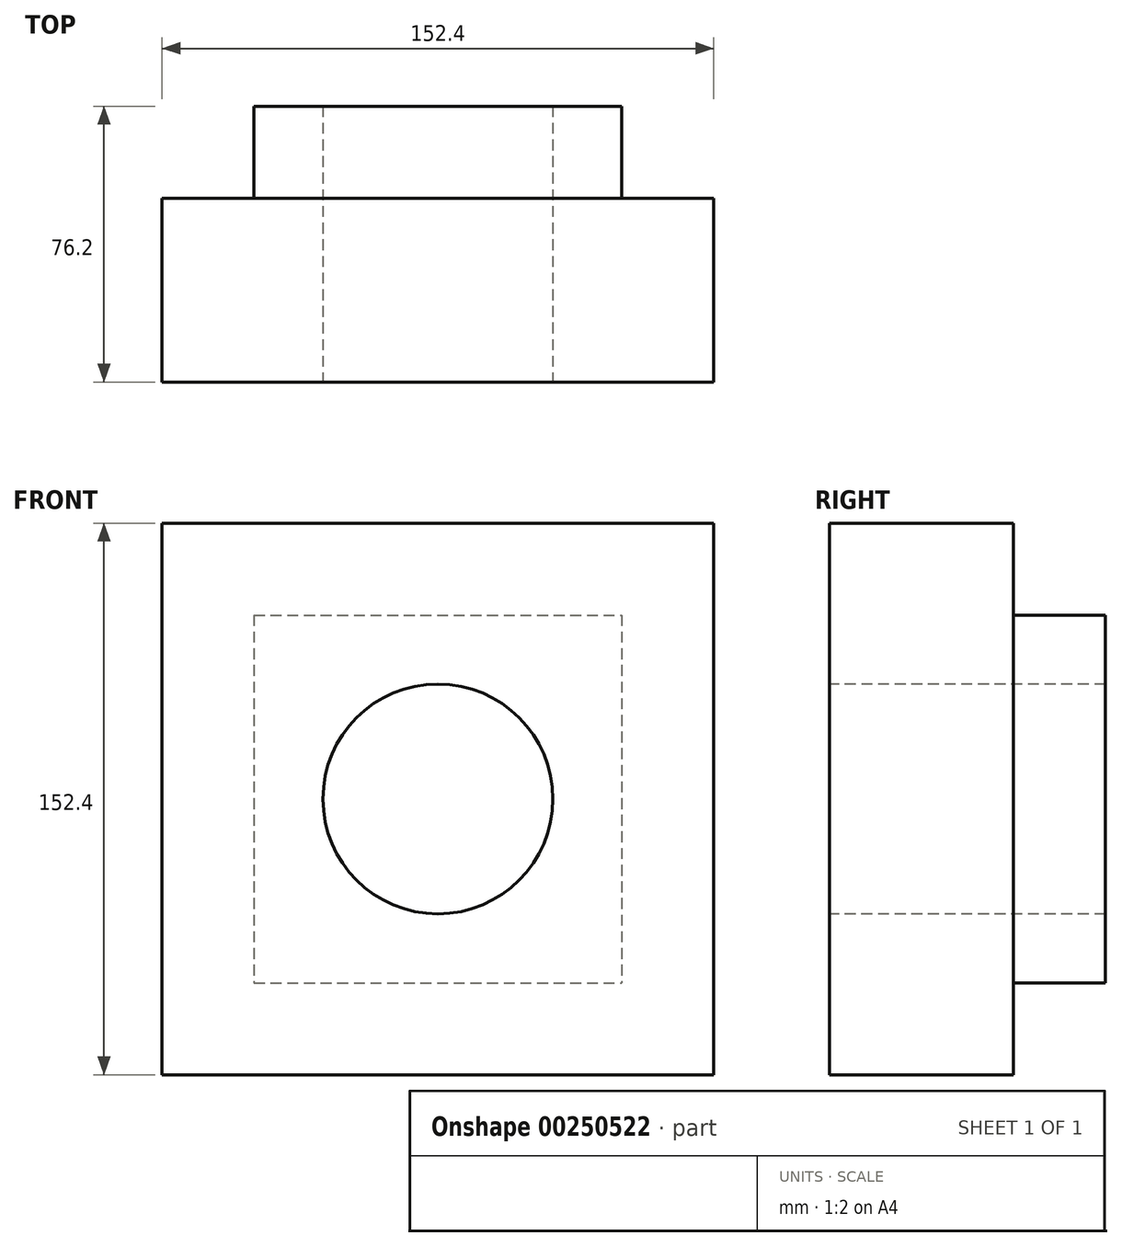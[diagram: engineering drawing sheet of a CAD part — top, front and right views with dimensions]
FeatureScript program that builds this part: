
annotation { "Feature Type Name" : "Feature", "Feature Type Description" : "" }
export const myFeature = defineFeature(function(context is Context, id is Id, definition is map)
    precondition{}
    {
        {
            var Q0;
            Q0=qCreatedBy(makeId("Front.planeOp"),FACE);
            var sketch = newSketch(context, id + "F0", { "sketchPlane" : qUnion([Q0])});
            skCircle(sketch, "E0", {"center": v(0, 0) * mm, "radius": 31.75 * mm});
            skLineSegment(sketch, "E1.bottom", {"start": v(-50.8, 50.8) * mm, "end": v(50.8, 50.8) * mm});
            skLineSegment(sketch, "E1.top", {"start": v(-50.8, -50.8) * mm, "end": v(50.8, -50.8) * mm});
            skLineSegment(sketch, "E1.left", {"start": v(-50.8, 50.8) * mm, "end": v(-50.8, -50.8) * mm});
            skLineSegment(sketch, "E1.right", {"start": v(50.8, 50.8) * mm, "end": v(50.8, -50.8) * mm});
            skLineSegment(sketch, "E2.bottom", {"start": v(-76.2, 76.2) * mm, "end": v(76.2, 76.2) * mm});
            skLineSegment(sketch, "E2.top", {"start": v(-76.2, -76.2) * mm, "end": v(76.2, -76.2) * mm});
            skLineSegment(sketch, "E2.left", {"start": v(-76.2, 76.2) * mm, "end": v(-76.2, -76.2) * mm});
            skLineSegment(sketch, "E2.right", {"start": v(76.2, 76.2) * mm, "end": v(76.2, -76.2) * mm});
            skSolve(sketch);
        }
        {
            var Q0;
            Q0=makeQuery(id+"F0.imprint","IMPRINT",FACE,{"disambiguationData":[TD([[makeQuery(id+"F0.imprint","IMPRINT",EDGE,{"derivedFrom":sQuery(id+"F0.wireOp",EDGE,"E0")}),-1.0]])]});
            extrude(context, id + "F1", {"entities" : qUnion([Q0]), "oppositeDirection" : true, "depth" : 76.2 * mm});
        }
        {
            var Q0;
            Q0=makeQuery(id+"F0.imprint","IMPRINT",FACE,{"disambiguationData":[TD([[makeQuery(id+"F0.imprint","IMPRINT",EDGE,{"derivedFrom":sQuery(id+"F0.wireOp",EDGE,"E1.bottom")}),1.0]])]});
            extrude(context, id + "F2", {"entities" : qUnion([Q0]), "operationType" : NewBodyOperationType.ADD, "oppositeDirection" : true, "depth" : 50.8 * mm});
        }
    });
